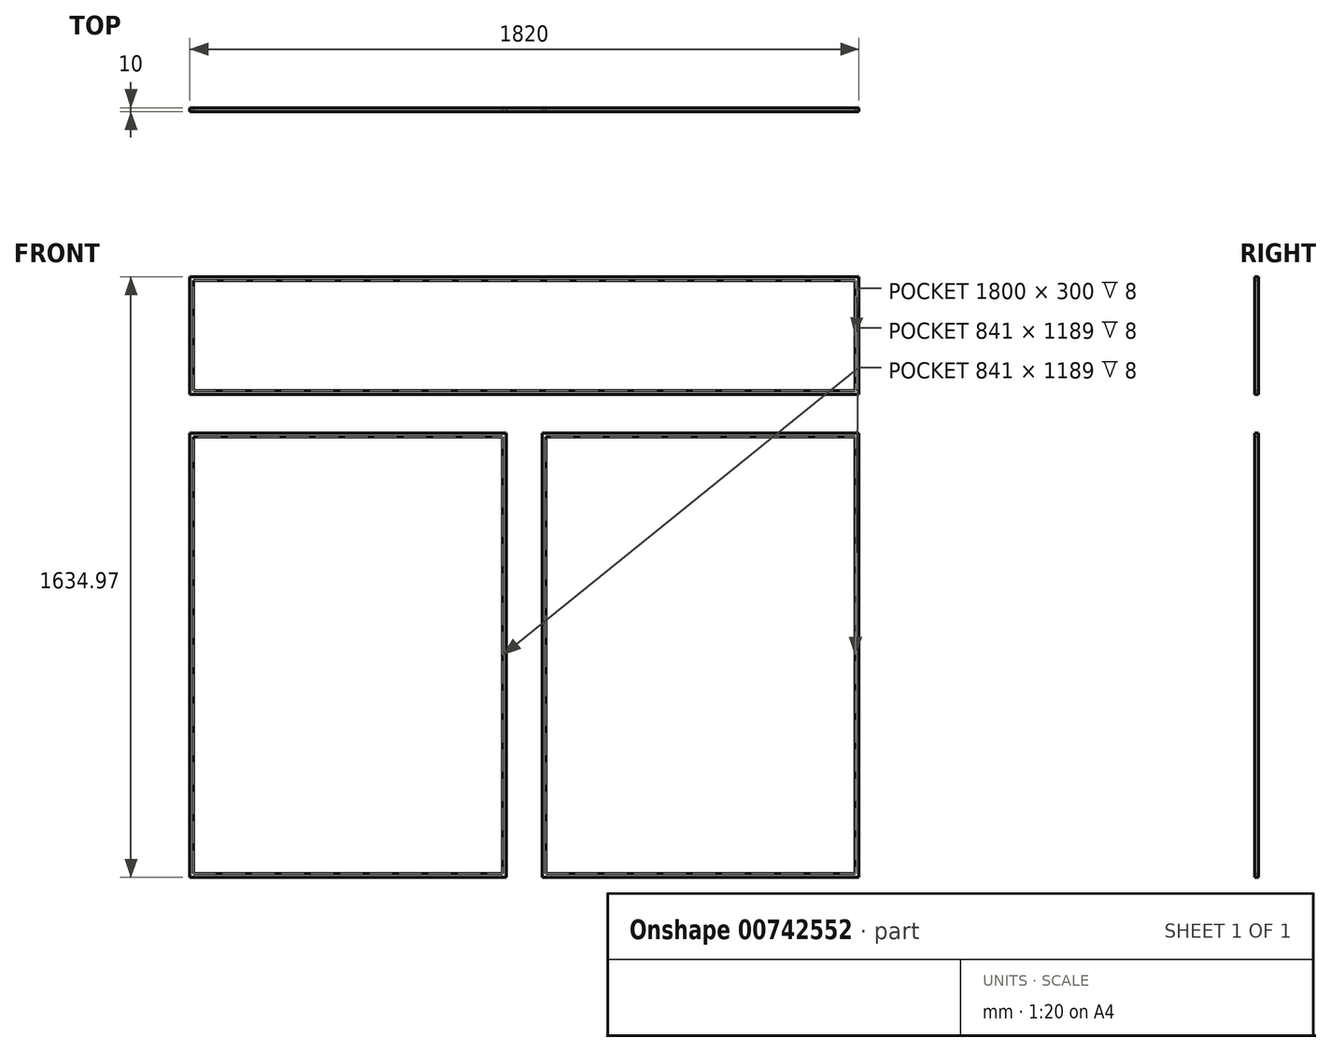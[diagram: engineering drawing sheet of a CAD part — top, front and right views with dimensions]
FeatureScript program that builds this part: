
annotation { "Feature Type Name" : "Feature", "Feature Type Description" : "" }
export const myFeature = defineFeature(function(context is Context, id is Id, definition is map)
    precondition{}
    {
        {
            var Q0;
            Q0=qCreatedBy(makeId("Front.planeOp"),FACE);
            var sketch = newSketch(context, id + "F0", { "sketchPlane" : qUnion([Q0])});
            skLineSegment(sketch, "E0.bottom", {"start": v(-792.8, 1132.2) * mm, "end": v(48.2, 1132.2) * mm});
            skLineSegment(sketch, "E0.top", {"start": v(-792.8, -56.8) * mm, "end": v(48.2, -56.8) * mm});
            skLineSegment(sketch, "E0.left", {"start": v(-792.8, 1132.2) * mm, "end": v(-792.8, -56.8) * mm});
            skLineSegment(sketch, "E0.right", {"start": v(48.2, 1132.2) * mm, "end": v(48.2, -56.8) * mm});
            skSolve(sketch);
        }
        {
            var Q0;
            Q0 = qSketchRegion(id + "F0", true);
            extrude(context, id + "F1", {"entities" : qUnion([Q0]), "depth" : 2 * mm, "offsetDistance" : 25 * mm});
        }
        {
            var Q0;
            Q0=makeQuery(id+"F1.opExtrude","CAP_FACE",FACE,{"disambiguationData":[OSD([sQuery(id+"F0.wireOp",EDGE,"E0.bottom"),sQuery(id+"F0.wireOp",EDGE,"E0.top"),sQuery(id+"F0.wireOp",EDGE,"E0.left"),sQuery(id+"F0.wireOp",EDGE,"E0.right")])],"isStart":true});
            var sketch = newSketch(context, id + "F2", { "sketchPlane" : qUnion([Q0])});
            skLineSegment(sketch, "E1.0", {"start": v(792.8, 1132.2) * mm, "end": v(-48.2, 1132.2) * mm});
            skLineSegment(sketch, "E1.1", {"start": v(792.8, 1132.2) * mm, "end": v(792.8, -56.8) * mm});
            skLineSegment(sketch, "E1.2", {"start": v(792.8, -56.8) * mm, "end": v(-48.2, -56.8) * mm});
            skLineSegment(sketch, "E1.3", {"start": v(-48.2, 1132.2) * mm, "end": v(-48.2, -56.8) * mm});
            skLineSegment(sketch, "E2.0", {"start": v(832.8, 1172.2) * mm, "end": v(-88.2, 1172.2) * mm});
            skLineSegment(sketch, "E2.1", {"start": v(832.8, 1172.2) * mm, "end": v(832.8, -96.8) * mm});
            skLineSegment(sketch, "E2.2", {"start": v(832.8, -96.8) * mm, "end": v(-88.2, -96.8) * mm});
            skLineSegment(sketch, "E2.3", {"start": v(-88.2, 1172.2) * mm, "end": v(-88.2, -96.8) * mm});
            skSolve(sketch);
        }
        {
            var Q0;
            Q0 = qSketchRegion(id + "F2", true);
            extrude(context, id + "F3", {"entities" : qUnion([Q0]), "operationType" : NewBodyOperationType.ADD, "oppositeDirection" : true, "depth" : 10 * mm, "offsetDistance" : 25 * mm});
        }
        {
            var Q0;
            Q0=makeQuery(id+"F3.opExtrude","SWEPT_FACE",FACE,{"disambiguationData":[OSD([sQuery(id+"F2.wireOp",EDGE,"E1.1")])]});
            cPlane(context, id + "F4", {"entities" : qUnion([Q0]), "cplaneType" : CPlaneType.OFFSET, "offset" : 900 * mm, "width" : 150 * mm, "height" : 150 * mm});
        }
        {
            var Q0;
            Q0=makeQuery(id+"F1.opExtrude","SWEPT_BODY",BODY,{"disambiguationData":[OSD([sQuery(id+"F0.wireOp",EDGE,"E0.bottom"),sQuery(id+"F0.wireOp",EDGE,"E0.top"),sQuery(id+"F0.wireOp",EDGE,"E0.left"),sQuery(id+"F0.wireOp",EDGE,"E0.right")])]});
            var Q1;
            Q1=qCreatedBy(id+"F4.planeOp",FACE);
            mirror(context, id + "F5", {"entities" : qUnion([Q0]), "mirrorPlane" : qUnion([Q1])});
        }
        {
            var Q0;
            Q0=makeQuery(id+"F3.opExtrude","CAP_FACE",FACE,{"disambiguationData":[OSD([sQuery(id+"F2.wireOp",EDGE,"E1.0"),sQuery(id+"F2.wireOp",EDGE,"E1.1"),sQuery(id+"F2.wireOp",EDGE,"E1.2"),sQuery(id+"F2.wireOp",EDGE,"E1.3"),sQuery(id+"F2.wireOp",EDGE,"E2.0"),sQuery(id+"F2.wireOp",EDGE,"E2.1"),sQuery(id+"F2.wireOp",EDGE,"E2.2"),sQuery(id+"F2.wireOp",EDGE,"E2.3")])],"isStart":false});
            var sketch = newSketch(context, id + "F6", { "sketchPlane" : qUnion([Q0])});
            skLineSegment(sketch, "E3.bottom", {"start": v(-832.8, 1218.17) * mm, "end": v(1047.2, 1218.17) * mm});
            skLineSegment(sketch, "E3.top", {"start": v(-832.8, 1598.17) * mm, "end": v(1047.2, 1598.17) * mm});
            skLineSegment(sketch, "E3.left", {"start": v(-832.8, 1218.17) * mm, "end": v(-832.8, 1598.17) * mm});
            skLineSegment(sketch, "E3.right", {"start": v(1047.2, 1218.17) * mm, "end": v(1047.2, 1598.17) * mm});
            skLineSegment(sketch, "E4.0", {"start": v(-792.8, 1258.17) * mm, "end": v(1007.2, 1258.17) * mm});
            skLineSegment(sketch, "E4.1", {"start": v(-792.8, 1258.17) * mm, "end": v(-792.8, 1558.17) * mm});
            skLineSegment(sketch, "E4.2", {"start": v(-792.8, 1558.17) * mm, "end": v(1007.2, 1558.17) * mm});
            skLineSegment(sketch, "E4.3", {"start": v(1007.2, 1258.17) * mm, "end": v(1007.2, 1558.17) * mm});
            skSolve(sketch);
        }
        {
            var Q0;
            Q0 = qSketchRegion(id + "F6", true);
            var Q1;
            Q1=makeQuery(id+"F3.boolean.opBoolean","MERGE",FACE,{"derivedFrom":[makeQuery(id+"F1.opExtrude","CAP_FACE",FACE,{"disambiguationData":[OSD([sQuery(id+"F0.wireOp",EDGE,"E0.bottom"),sQuery(id+"F0.wireOp",EDGE,"E0.top"),sQuery(id+"F0.wireOp",EDGE,"E0.left"),sQuery(id+"F0.wireOp",EDGE,"E0.right")])],"isStart":true}),makeQuery(id+"F3.opExtrude","CAP_FACE",FACE,{"disambiguationData":[OSD([sQuery(id+"F2.wireOp",EDGE,"E1.0"),sQuery(id+"F2.wireOp",EDGE,"E1.1"),sQuery(id+"F2.wireOp",EDGE,"E1.2"),sQuery(id+"F2.wireOp",EDGE,"E1.3"),sQuery(id+"F2.wireOp",EDGE,"E2.0"),sQuery(id+"F2.wireOp",EDGE,"E2.1"),sQuery(id+"F2.wireOp",EDGE,"E2.2"),sQuery(id+"F2.wireOp",EDGE,"E2.3")])],"isStart":true})]});
            extrude(context, id + "F7", {"entities" : qUnion([Q0]), "endBound" : BoundingType.UP_TO_SURFACE, "oppositeDirection" : true, "depth" : 25 * mm, "endBoundEntityFace" : qUnion([Q1]), "offsetDistance" : 25 * mm});
        }
        {
            var Q0;
            Q0=makeQuery(id+"F1.opExtrude","CAP_FACE",FACE,{"disambiguationData":[OSD([sQuery(id+"F0.wireOp",EDGE,"E0.bottom"),sQuery(id+"F0.wireOp",EDGE,"E0.top"),sQuery(id+"F0.wireOp",EDGE,"E0.left"),sQuery(id+"F0.wireOp",EDGE,"E0.right")])],"isStart":false});
            var sketch = newSketch(context, id + "F8", { "sketchPlane" : qUnion([Q0])});
            skLineSegment(sketch, "E5.0", {"start": v(1007.2, 1558.17) * mm, "end": v(1007.2, 1258.17) * mm});
            skLineSegment(sketch, "E5.1", {"start": v(1007.2, 1258.17) * mm, "end": v(-792.8, 1258.17) * mm});
            skLineSegment(sketch, "E5.2", {"start": v(1007.2, 1558.17) * mm, "end": v(-792.8, 1558.17) * mm});
            skLineSegment(sketch, "E5.3", {"start": v(-792.8, 1558.17) * mm, "end": v(-792.8, 1258.17) * mm});
            skSolve(sketch);
        }
        {
            var Q0;
            Q0 = qSketchRegion(id + "F8", true);
            var Q1;
            Q1=makeQuery(id+"F3.boolean.opBoolean","MERGE",FACE,{"derivedFrom":[makeQuery(id+"F1.opExtrude","CAP_FACE",FACE,{"disambiguationData":[OSD([sQuery(id+"F0.wireOp",EDGE,"E0.bottom"),sQuery(id+"F0.wireOp",EDGE,"E0.top"),sQuery(id+"F0.wireOp",EDGE,"E0.left"),sQuery(id+"F0.wireOp",EDGE,"E0.right")])],"isStart":true}),makeQuery(id+"F3.opExtrude","CAP_FACE",FACE,{"disambiguationData":[OSD([sQuery(id+"F2.wireOp",EDGE,"E1.0"),sQuery(id+"F2.wireOp",EDGE,"E1.1"),sQuery(id+"F2.wireOp",EDGE,"E1.2"),sQuery(id+"F2.wireOp",EDGE,"E1.3"),sQuery(id+"F2.wireOp",EDGE,"E2.0"),sQuery(id+"F2.wireOp",EDGE,"E2.1"),sQuery(id+"F2.wireOp",EDGE,"E2.2"),sQuery(id+"F2.wireOp",EDGE,"E2.3")])],"isStart":true})]});
            extrude(context, id + "F9", {"entities" : qUnion([Q0]), "operationType" : NewBodyOperationType.ADD, "endBound" : BoundingType.UP_TO_SURFACE, "oppositeDirection" : true, "depth" : 25 * mm, "endBoundEntityFace" : qUnion([Q1]), "offsetDistance" : 25 * mm});
        }
        {
            var Q0;
            Q0=makeQuery(id+"F7.opExtrude","CAP_FACE",FACE,{"disambiguationData":[OSD([sQuery(id+"F6.wireOp",EDGE,"E3.bottom"),sQuery(id+"F6.wireOp",EDGE,"E3.top"),sQuery(id+"F6.wireOp",EDGE,"E3.left"),sQuery(id+"F6.wireOp",EDGE,"E3.right"),sQuery(id+"F6.wireOp",EDGE,"E4.0"),sQuery(id+"F6.wireOp",EDGE,"E4.1"),sQuery(id+"F6.wireOp",EDGE,"E4.2"),sQuery(id+"F6.wireOp",EDGE,"E4.3")])],"isStart":true});
            var sketch = newSketch(context, id + "F10", { "sketchPlane" : qUnion([Q0])});
            skLineSegment(sketch, "E6.bottom", {"start": v(-802.8, 1568.17) * mm, "end": v(1017.2, 1568.17) * mm});
            skLineSegment(sketch, "E6.top", {"start": v(-802.8, -66.8) * mm, "end": v(1017.2, -66.8) * mm});
            skLineSegment(sketch, "E6.left", {"start": v(-802.8, 1568.17) * mm, "end": v(-802.8, -66.8) * mm});
            skLineSegment(sketch, "E6.right", {"start": v(1017.2, 1568.17) * mm, "end": v(1017.2, -66.8) * mm});
            skLineSegment(sketch, "E7.bottom", {"start": v(-832.8, 1598.17) * mm, "end": v(1075.65, 1598.17) * mm});
            skLineSegment(sketch, "E7.top", {"start": v(-832.8, -126.36) * mm, "end": v(1075.65, -126.36) * mm});
            skLineSegment(sketch, "E7.left", {"start": v(-832.8, 1598.17) * mm, "end": v(-832.8, -126.36) * mm});
            skLineSegment(sketch, "E7.right", {"start": v(1075.65, 1598.17) * mm, "end": v(1075.65, -126.36) * mm});
            skSolve(sketch);
        }
        {
            var Q0;
            Q0 = qSketchRegion(id + "F10", true);
            extrude(context, id + "F11", {"entities" : qUnion([Q0]), "operationType" : NewBodyOperationType.REMOVE, "oppositeDirection" : true, "depth" : 25 * mm, "offsetDistance" : 25 * mm});
        }
        {
            var Q0;
            Q0=makeQuery(id+"F7.opExtrude","CAP_FACE",FACE,{"disambiguationData":[OSD([sQuery(id+"F6.wireOp",EDGE,"E3.bottom"),sQuery(id+"F6.wireOp",EDGE,"E3.top"),sQuery(id+"F6.wireOp",EDGE,"E3.left"),sQuery(id+"F6.wireOp",EDGE,"E3.right"),sQuery(id+"F6.wireOp",EDGE,"E4.0"),sQuery(id+"F6.wireOp",EDGE,"E4.1"),sQuery(id+"F6.wireOp",EDGE,"E4.2"),sQuery(id+"F6.wireOp",EDGE,"E4.3")])],"isStart":true});
            var sketch = newSketch(context, id + "F12", { "sketchPlane" : qUnion([Q0])});
            skLineSegment(sketch, "E8.bottom", {"start": v(-802.8, 1248.17) * mm, "end": v(1017.2, 1248.17) * mm});
            skLineSegment(sketch, "E8.top", {"start": v(-802.8, 1142.2) * mm, "end": v(1017.2, 1142.2) * mm});
            skLineSegment(sketch, "E8.left", {"start": v(-802.8, 1248.17) * mm, "end": v(-802.8, 1142.2) * mm});
            skLineSegment(sketch, "E8.right", {"start": v(1017.2, 1248.17) * mm, "end": v(1017.2, 1142.2) * mm});
            skSolve(sketch);
        }
        {
            var Q0;
            Q0 = qSketchRegion(id + "F12", true);
            extrude(context, id + "F13", {"entities" : qUnion([Q0]), "operationType" : NewBodyOperationType.REMOVE, "oppositeDirection" : true, "depth" : 25 * mm, "offsetDistance" : 25 * mm});
        }
        {
            var Q0;
            Q0=makeQuery(id+"F5.opPattern","COPY",FACE,{"derivedFrom":makeQuery(id+"F3.opExtrude","CAP_FACE",FACE,{"disambiguationData":[OSD([sQuery(id+"F2.wireOp",EDGE,"E1.0"),sQuery(id+"F2.wireOp",EDGE,"E1.1"),sQuery(id+"F2.wireOp",EDGE,"E1.2"),sQuery(id+"F2.wireOp",EDGE,"E1.3"),sQuery(id+"F2.wireOp",EDGE,"E2.0"),sQuery(id+"F2.wireOp",EDGE,"E2.1"),sQuery(id+"F2.wireOp",EDGE,"E2.2"),sQuery(id+"F2.wireOp",EDGE,"E2.3")])],"isStart":false}),"instanceName":"1"});
            var sketch = newSketch(context, id + "F14", { "sketchPlane" : qUnion([Q0])});
            skLineSegment(sketch, "E9.bottom", {"start": v(58.2, 1142.2) * mm, "end": v(156.2, 1142.2) * mm});
            skLineSegment(sketch, "E9.top", {"start": v(58.2, -66.8) * mm, "end": v(156.2, -66.8) * mm});
            skLineSegment(sketch, "E9.left", {"start": v(58.2, 1142.2) * mm, "end": v(58.2, -66.8) * mm});
            skLineSegment(sketch, "E9.right", {"start": v(156.2, 1142.2) * mm, "end": v(156.2, -66.8) * mm});
            skSolve(sketch);
        }
        {
            var Q0;
            Q0 = qSketchRegion(id + "F14", true);
            extrude(context, id + "F15", {"entities" : qUnion([Q0]), "operationType" : NewBodyOperationType.REMOVE, "oppositeDirection" : true, "depth" : 25 * mm, "offsetDistance" : 25 * mm});
        }
    });
